# Revit family: BIMLIB_Коллектор_802_7_РОСТерм
name_source: partatom
category: Оборудование
revit_build: Autodesk Revit 2017 (Build: 20170118_1100(x64)
units: mm (PartAtom-declared; Revit-internal decimal feet)

## family parameters
Всегда вертикально = Да
На основе рабочей плоскости = Нет
Общий = Нет
При загрузке вырезать с полостями = Нет
Размер круглого соединителя = Использовать диаметр
Тип детали = Нормальный
Точка расчета площади = Нет

## types (2) — shared parameters
ADSK_URL документации изделия = http://rostherm.ru
ADSK_URL страницы изделия = http://rostherm.ru
ADSK_Версия Revit = 2017
ADSK_Единица измерения = шт.
ADSK_Завод-изготовитель = Heizen
ADSK_Марка = HEIZEN 802
ADSK_Материал = BIMLIB_Cталь_РТ
ADSK_Обозначение = ГОСТ 12.2.063-2015
BL_BIM library = https://bimlib.pro
URL = http://rostherm.ru
Изготовитель = РОСТерм
Описание = Коллекторная группа для систем напольного отопления
РТ_DN2 = 20 мм
РТ_DN3 = 15 мм
РТ_R/2 = 10 мм
zero-valued in all types: ADSK_Масса

## per-type parameters (varying)
| type | ADSK_Код изделия | ADSK_Наименование краткое | РТ_DN1 | РТ_R1 |
| Коллекторная группа HEIZEN 802 для систем напольного отопления Ду32 на 7 выходов | 802-32-05-07 | HEIZEN 802 Ду32 на 7 выходов | 32 мм | 16 мм |
| Коллекторная группа HEIZEN 802 для систем напольного отопления Ду40 на 7 выходов | 802-40-05-07 | HEIZEN 802 Ду40 на 7 выходов | 40 мм | 20 мм |

note: column(s) folded — value = type name in every type: ADSK_Наименование

## geometry (parser evidence)
native form markers: Sweep x2
no freeform markers — native parametric forms only
